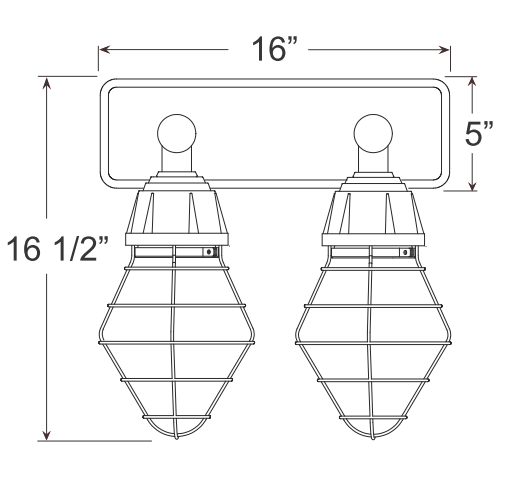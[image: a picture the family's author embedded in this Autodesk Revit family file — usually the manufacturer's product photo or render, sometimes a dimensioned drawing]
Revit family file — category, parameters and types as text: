
# Revit family: VBURGUP110
name_source: partatom
category: Lighting Fixtures
units: mm (PartAtom-declared; Revit-internal decimal feet)

## family parameters
Always vertical = Yes
Cut with Voids When Loaded = No
Light Source = Yes
OmniClass Number = 23.80.70.00
OmniClass Title = Lighting
Part Type = Normal
Room Calculation Point = No
Round Connector Dimension = Use Diameter
Shared = No
Work Plane-Based = No

## types (3) — shared parameters
Apparent Load = 200 VA
Body Colour = cast aluminium
Body Material = body
Bulb = Bulb
Color Filter = 16777215
Construction Material = cast aluminum.
Default Elevation = 0' - 0"
Description = 120-277 Voltage
Dimming Lamp Color Temperature Shift = <None>
INSIDE BODY = INSIDE BODY
Load Classification = Lighting
Manufacturer = ANP Lighting
Photometric Web File = generic.ies
Power Factor = 1
Tilt Angle = 90.00°
URL = https://www.anplighting.com
Voltage = 120 V
Warranty = 5 year limited warranty
Wattage Comments = 200W Max

## per-type parameters (varying)
| type | Fixture Diameter | Fixture Height | Lamp | Model | Weight |
| VBURGUP110-1 | 0' - 8" | 1' - 4 1/2" | Incandescent | VBURGUP110-1 | 4.2 lbs |
| VBURGUP110-2 | 16' - 0" | 1' - 4 1/2" | Incandescent | VBURGUP110-2 | 5.9 lbs |
| VBURGUP110-3 | 2' - 1" | 1' - 3" | Incandescent
 Incandescent | VBURGUP120-3 | 14.5 lbs |

type visibility flags: 3 boolean params named "<type name>" — each type sets only its own to Yes (folded from table)

## geometry (parser evidence)
native form markers: Sweep x7
no freeform markers — native parametric forms only
